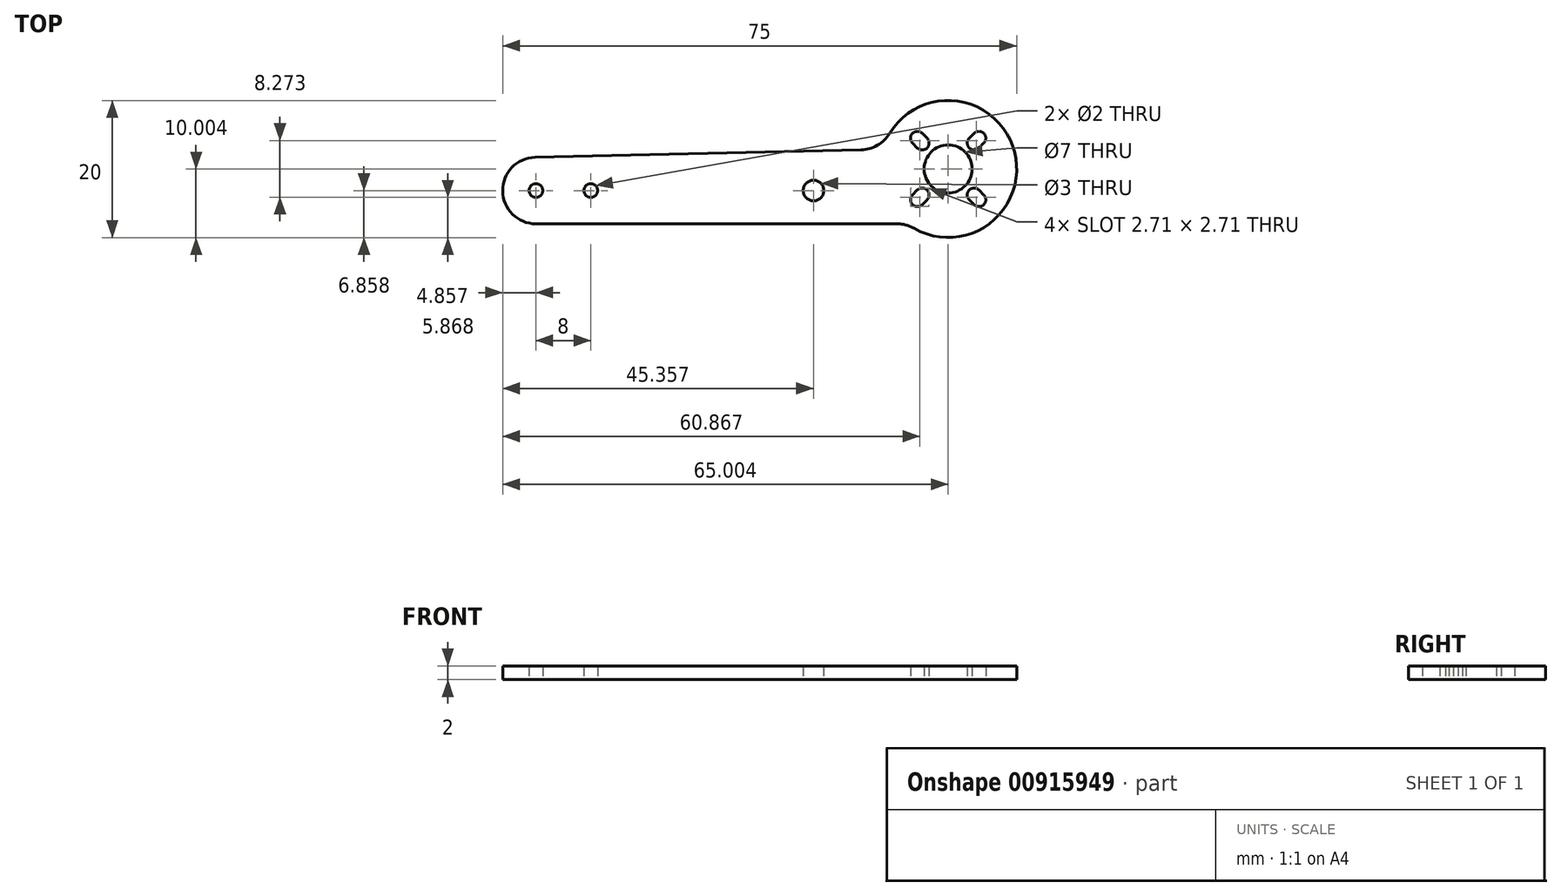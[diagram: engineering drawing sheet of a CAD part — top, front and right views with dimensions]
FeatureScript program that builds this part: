
annotation { "Feature Type Name" : "Feature", "Feature Type Description" : "" }
export const myFeature = defineFeature(function(context is Context, id is Id, definition is map)
    precondition{}
    {
        {
            var Q0;
            Q0=qCreatedBy(makeId("Top.planeOp"),FACE);
            var sketch = newSketch(context, id + "F0", { "sketchPlane" : qUnion([Q0])});
            skLineSegment(sketch, "E0.bottom", {"start": v(-113.47, 5.28) * mm, "end": v(-38.47, 5.28) * mm, "construction": true});
            skLineSegment(sketch, "E0.top", {"start": v(-113.47, -14.72) * mm, "end": v(-38.47, -14.72) * mm, "construction": true});
            skLineSegment(sketch, "E0.left", {"start": v(-113.47, 5.28) * mm, "end": v(-113.47, -14.72) * mm, "construction": true});
            skLineSegment(sketch, "E0.right", {"start": v(-38.47, 5.28) * mm, "end": v(-38.47, -14.72) * mm, "construction": true});
            skArc(sketch, "E1", {"start": v(-53.46, -13.38) * mm, "mid": v(-38.78, -2.23) * mm, "end": v(-57.01, 0.48) * mm});
            skCircle(sketch, "E2", {"center": v(-48.47, -4.72) * mm, "radius": 3.5 * mm});
            skCircle(sketch, "E3", {"center": v(-48.47, -4.72) * mm, "radius": 4.35 * mm, "construction": true});
            skLineSegment(sketch, "E4", {"start": v(-38.47, 5.28) * mm, "end": v(-48.47, -4.72) * mm, "construction": true});
            skLineSegment(sketch, "E5", {"start": v(-38.47, -14.72) * mm, "end": v(-48.47, -4.72) * mm, "construction": true});
            skArc(sketch, "E6", {"start": v(-45.4, -0.23) * mm, "mid": v(-45.4, -1.64) * mm, "end": v(-43.98, -1.64) * mm});
            skArc(sketch, "E7", {"start": v(-43.27, -0.93) * mm, "mid": v(-43.27, 0.48) * mm, "end": v(-44.68, 0.48) * mm});
            skLineSegment(sketch, "E8", {"start": v(-44.68, 0.48) * mm, "end": v(-45.4, -0.23) * mm});
            skLineSegment(sketch, "E9", {"start": v(-43.98, -1.64) * mm, "end": v(-43.27, -0.93) * mm});
            skArc(sketch, "E10.1.0", {"start": v(-52.25, 0.48) * mm, "mid": v(-53.66, 0.48) * mm, "end": v(-53.66, -0.93) * mm});
            skLineSegment(sketch, "E10.1.1", {"start": v(-51.54, -0.23) * mm, "end": v(-52.25, 0.48) * mm});
            skArc(sketch, "E10.1.2", {"start": v(-52.96, -1.64) * mm, "mid": v(-51.54, -1.64) * mm, "end": v(-51.54, -0.23) * mm});
            skLineSegment(sketch, "E10.1.3", {"start": v(-53.66, -0.93) * mm, "end": v(-52.96, -1.64) * mm});
            skArc(sketch, "E10.2.0", {"start": v(-53.66, -8.5) * mm, "mid": v(-53.66, -9.91) * mm, "end": v(-52.25, -9.91) * mm});
            skLineSegment(sketch, "E10.2.1", {"start": v(-52.96, -7.8) * mm, "end": v(-53.66, -8.5) * mm});
            skArc(sketch, "E10.2.2", {"start": v(-51.54, -9.2) * mm, "mid": v(-51.54, -7.8) * mm, "end": v(-52.96, -7.8) * mm});
            skLineSegment(sketch, "E10.2.3", {"start": v(-52.25, -9.91) * mm, "end": v(-51.54, -9.2) * mm});
            skArc(sketch, "E10.3.0", {"start": v(-44.68, -9.91) * mm, "mid": v(-43.27, -9.91) * mm, "end": v(-43.27, -8.5) * mm});
            skLineSegment(sketch, "E10.3.1", {"start": v(-45.4, -9.2) * mm, "end": v(-44.68, -9.91) * mm});
            skArc(sketch, "E10.3.2", {"start": v(-43.98, -7.8) * mm, "mid": v(-45.4, -7.8) * mm, "end": v(-45.4, -9.2) * mm});
            skLineSegment(sketch, "E10.3.3", {"start": v(-43.27, -8.5) * mm, "end": v(-43.98, -7.8) * mm});
            skLineSegment(sketch, "E11", {"start": v(-113.47, -3.12) * mm, "end": v(-113.47, -12.72) * mm, "construction": true});
            skLineSegment(sketch, "E12", {"start": v(-113.47, -12.72) * mm, "end": v(-59.47, -12.72) * mm, "construction": true});
            skLineSegment(sketch, "E13", {"start": v(-59.47, -1.92) * mm, "end": v(-113.47, -3.12) * mm, "construction": true});
            skArc(sketch, "E14", {"start": v(-108.72, -3.01) * mm, "mid": v(-113.47, -7.92) * mm, "end": v(-108.61, -12.72) * mm});
            skLineSegment(sketch, "E15", {"start": v(-108.72, -3.01) * mm, "end": v(-61.17, -1.92) * mm});
            skLineSegment(sketch, "E16", {"start": v(-108.61, -12.72) * mm, "end": v(-55.95, -12.72) * mm});
            skCircle(sketch, "E17", {"center": v(-108.61, -7.86) * mm, "radius": 1 * mm});
            skLineSegment(sketch, "E18", {"start": v(-108.61, -7.86) * mm, "end": v(-100.61, -7.86) * mm, "construction": true});
            skLineSegment(sketch, "E19", {"start": v(-100.61, -7.86) * mm, "end": v(-68.11, -7.86) * mm, "construction": true});
            skCircle(sketch, "E20", {"center": v(-100.61, -7.86) * mm, "radius": 1 * mm});
            skCircle(sketch, "E21", {"center": v(-68.11, -7.86) * mm, "radius": 1.5 * mm});
            skPoint(sketch, "E22.visualSharp", {"position": v(-58.05, -1.85) * mm});
            skArc(sketch, "E22.filletArc", {"start": v(-61.17, -1.92) * mm, "mid": v(-58.78, -1.25) * mm, "end": v(-57.01, 0.48) * mm});
            skPoint(sketch, "E23.visualSharp", {"position": v(-54.47, -12.72) * mm});
            skArc(sketch, "E23.filletArc", {"start": v(-53.46, -13.38) * mm, "mid": v(-54.66, -12.89) * mm, "end": v(-55.95, -12.72) * mm});
            skSolve(sketch);
        }
        {
            var Q0;
            Q0=makeQuery(id+"F0.imprint","IMPRINT",FACE,{"disambiguationData":[TD([[makeQuery(id+"F0.imprint","IMPRINT",EDGE,{"derivedFrom":sQuery(id+"F0.wireOp",EDGE,"E1")}),1.0]])]});
            extrude(context, id + "F1", {"entities" : qUnion([Q0]), "depth" : 2 * mm, "offsetDistance" : 25 * mm});
        }
    });
